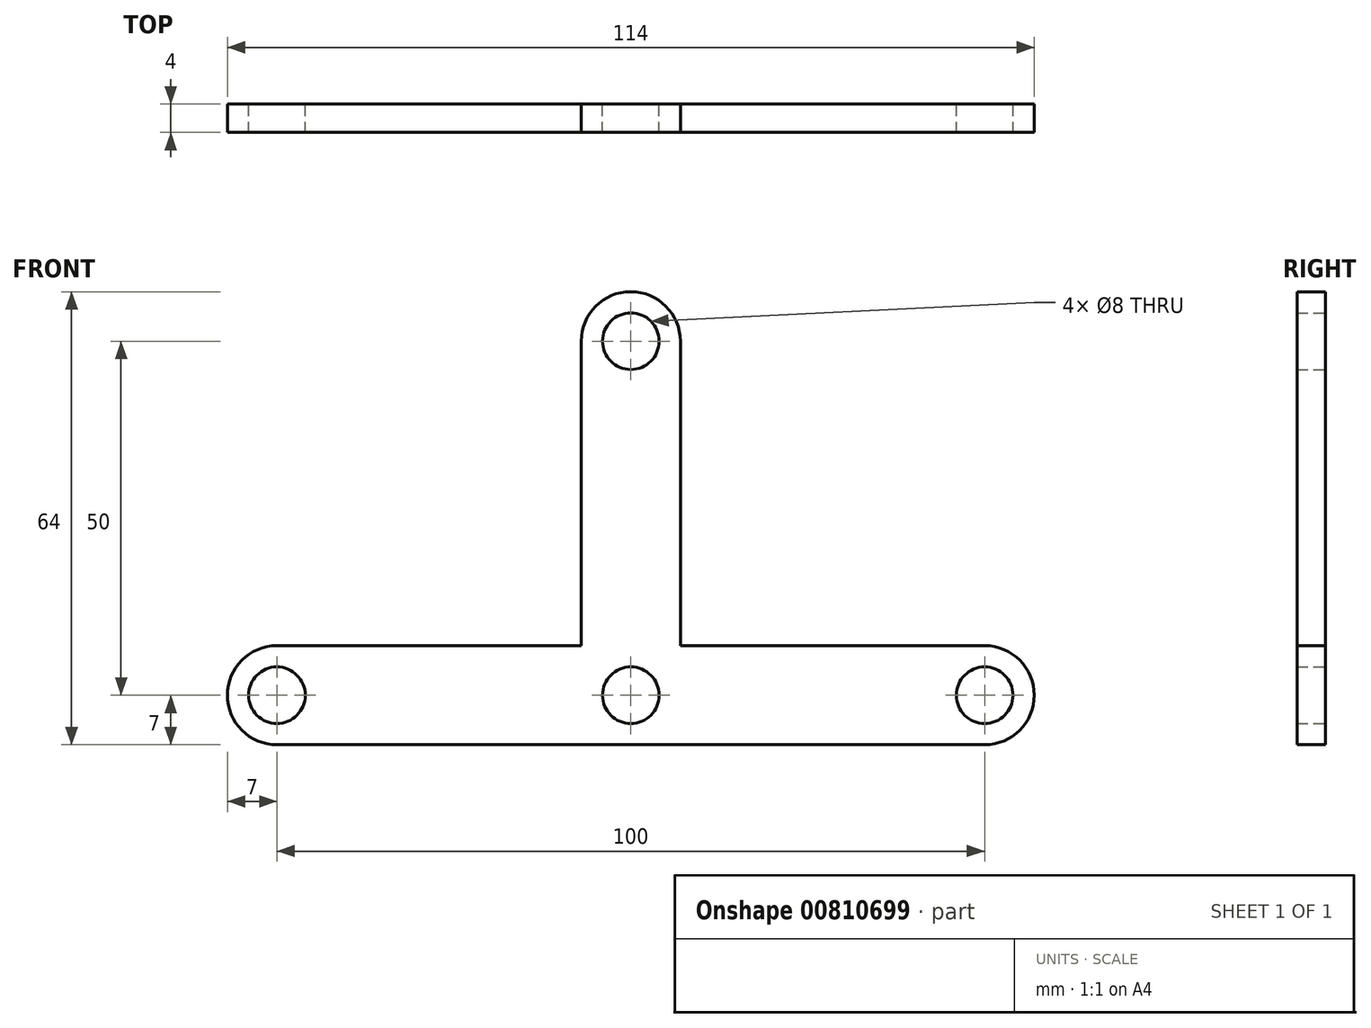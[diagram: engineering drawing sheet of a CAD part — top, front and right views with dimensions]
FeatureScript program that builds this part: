
annotation { "Feature Type Name" : "Feature", "Feature Type Description" : "" }
export const myFeature = defineFeature(function(context is Context, id is Id, definition is map)
    precondition{}
    {
        {
            var Q0;
            Q0=qCreatedBy(makeId("Front.planeOp"),FACE);
            var sketch = newSketch(context, id + "F0", { "sketchPlane" : qUnion([Q0])});
            skLineSegment(sketch, "E0", {"start": v(-7, 57) * mm, "end": v(7, 57) * mm});
            skLineSegment(sketch, "E1", {"start": v(7, 57) * mm, "end": v(7, 7) * mm});
            skLineSegment(sketch, "E2", {"start": v(7, 7) * mm, "end": v(57, 7) * mm});
            skLineSegment(sketch, "E3", {"start": v(57, 7) * mm, "end": v(57, -7) * mm});
            skLineSegment(sketch, "E4", {"start": v(57, -7) * mm, "end": v(-57, -7) * mm});
            skLineSegment(sketch, "E5", {"start": v(-57, -7) * mm, "end": v(-57, 7) * mm});
            skLineSegment(sketch, "E6", {"start": v(-57, 7) * mm, "end": v(-7, 7) * mm});
            skLineSegment(sketch, "E7", {"start": v(-7, 7) * mm, "end": v(-7, 57) * mm});
            skLineSegment(sketch, "E8", {"start": v(-43.9, 50) * mm, "end": v(24.17, 50) * mm, "construction": true});
            skLineSegment(sketch, "E9", {"start": v(-50, 9.78) * mm, "end": v(-50, -16.16) * mm, "construction": true});
            skLineSegment(sketch, "E10", {"start": v(50, 11.98) * mm, "end": v(50, -15.06) * mm, "construction": true});
            skCircle(sketch, "E11", {"center": v(0, 50) * mm, "radius": 4 * mm});
            skCircle(sketch, "E12", {"center": v(50, 0) * mm, "radius": 4 * mm});
            skCircle(sketch, "E13", {"center": v(-50, 0) * mm, "radius": 4 * mm});
            skPoint(sketch, "E13.centerSnap0", {"position": v(-57, 0) * mm});
            skCircle(sketch, "E14", {"center": v(0, 0) * mm, "radius": 4 * mm});
            skSolve(sketch);
        }
        {
            var Q0;
            Q0=makeQuery(id+"F0.imprint","IMPRINT",FACE,{"disambiguationData":[TD([[makeQuery(id+"F0.imprint","IMPRINT",EDGE,{"derivedFrom":sQuery(id+"F0.wireOp",EDGE,"E0")}),-1.0]])]});
            var Q1;
            Q1 = qSketchRegion(id + "FNNeJplIbe6vDNl_1", true);
            extrude(context, id + "F1", {"entities" : qUnion([Q0, Q1]), "depth" : 4 * mm, "offsetDistance" : 25 * mm});
        }
        {
            var Q0;
            Q0=makeQuery(id+"F1.opExtrude","SWEPT_EDGE",EDGE,{"disambiguationData":[OSD([sQuery(id+"F0.wireOp",EDGE,"E3"),sQuery(id+"F0.wireOp",EDGE,"E4")])]});
            var Q1;
            Q1=makeQuery(id+"F1.opExtrude","SWEPT_EDGE",EDGE,{"disambiguationData":[OSD([sQuery(id+"F0.wireOp",EDGE,"E2"),sQuery(id+"F0.wireOp",EDGE,"E3")])]});
            var Q2;
            Q2=makeQuery(id+"F1.opExtrude","SWEPT_EDGE",EDGE,{"disambiguationData":[OSD([sQuery(id+"F0.wireOp",EDGE,"E0"),sQuery(id+"F0.wireOp",EDGE,"E1")])]});
            var Q3;
            Q3=makeQuery(id+"F1.opExtrude","SWEPT_EDGE",EDGE,{"disambiguationData":[OSD([sQuery(id+"F0.wireOp",EDGE,"E0"),sQuery(id+"F0.wireOp",EDGE,"E7")])]});
            var Q4;
            Q4=makeQuery(id+"F1.opExtrude","SWEPT_EDGE",EDGE,{"disambiguationData":[OSD([sQuery(id+"F0.wireOp",EDGE,"E5"),sQuery(id+"F0.wireOp",EDGE,"E6")])]});
            var Q5;
            Q5=makeQuery(id+"F1.opExtrude","SWEPT_EDGE",EDGE,{"disambiguationData":[OSD([sQuery(id+"F0.wireOp",EDGE,"E4"),sQuery(id+"F0.wireOp",EDGE,"E5")])]});
            fillet(context, id + "F2", {"entities" : qUnion([Q0, Q1, Q2, Q3, Q4, Q5]), "radius" : 7 * mm, "tangentPropagation" : true, "allowEdgeOverflow" : false});
        }
    });
